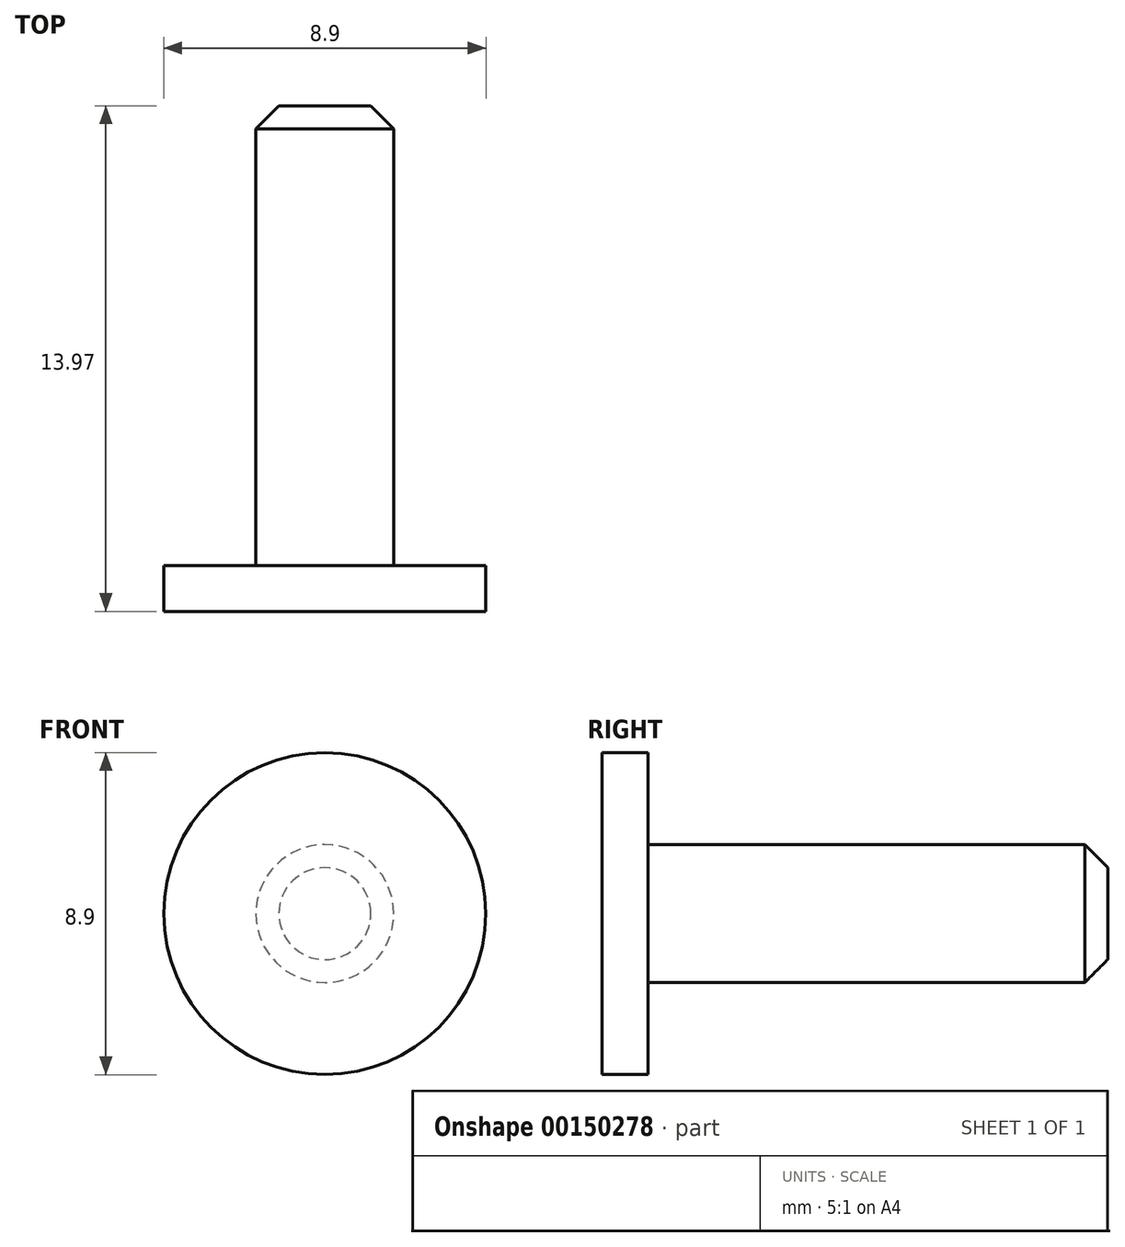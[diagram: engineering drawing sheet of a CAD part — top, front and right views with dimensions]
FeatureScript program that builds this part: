
annotation { "Feature Type Name" : "Feature", "Feature Type Description" : "" }
export const myFeature = defineFeature(function(context is Context, id is Id, definition is map)
    precondition{}
    {
        {
            var Q0;
            Q0=qCreatedBy(makeId("Front.planeOp"),FACE);
            var sketch = newSketch(context, id + "F0", { "sketchPlane" : qUnion([Q0])});
            skCircle(sketch, "E0", {"center": v(0, 0) * mm, "radius": 1.9 * mm});
            skSolve(sketch);
        }
        {
            var Q0;
            Q0 = qSketchRegion(id + "F0", true);
            extrude(context, id + "F1", {"entities" : qUnion([Q0]), "depth" : 12.7 * mm});
        }
        {
            var Q0;
            Q0=makeQuery(id+"F1.opExtrude","CAP_FACE",FACE,{"disambiguationData":[OSD([sQuery(id+"F0.wireOp",EDGE,"E0")])],"isStart":false});
            var sketch = newSketch(context, id + "F2", { "sketchPlane" : qUnion([Q0])});
            skCircle(sketch, "E1", {"center": v(0, 0) * mm, "radius": 4.45 * mm});
            skSolve(sketch);
        }
        {
            var Q0;
            Q0 = qSketchRegion(id + "F2", true);
            extrude(context, id + "F3", {"entities" : qUnion([Q0]), "operationType" : NewBodyOperationType.ADD, "depth" : 1.27 * mm});
        }
        {
            var Q0;
            Q0=makeQuery(id+"F1.opExtrude","CAP_EDGE",EDGE,{"disambiguationData":[OSD([sQuery(id+"F0.wireOp",EDGE,"E0")])],"isStart":true});
            chamfer(context, id + "F4", {"entities" : qUnion([Q0]), "width" : 0.64 * mm, "tangentPropagation" : true});
        }
    });
